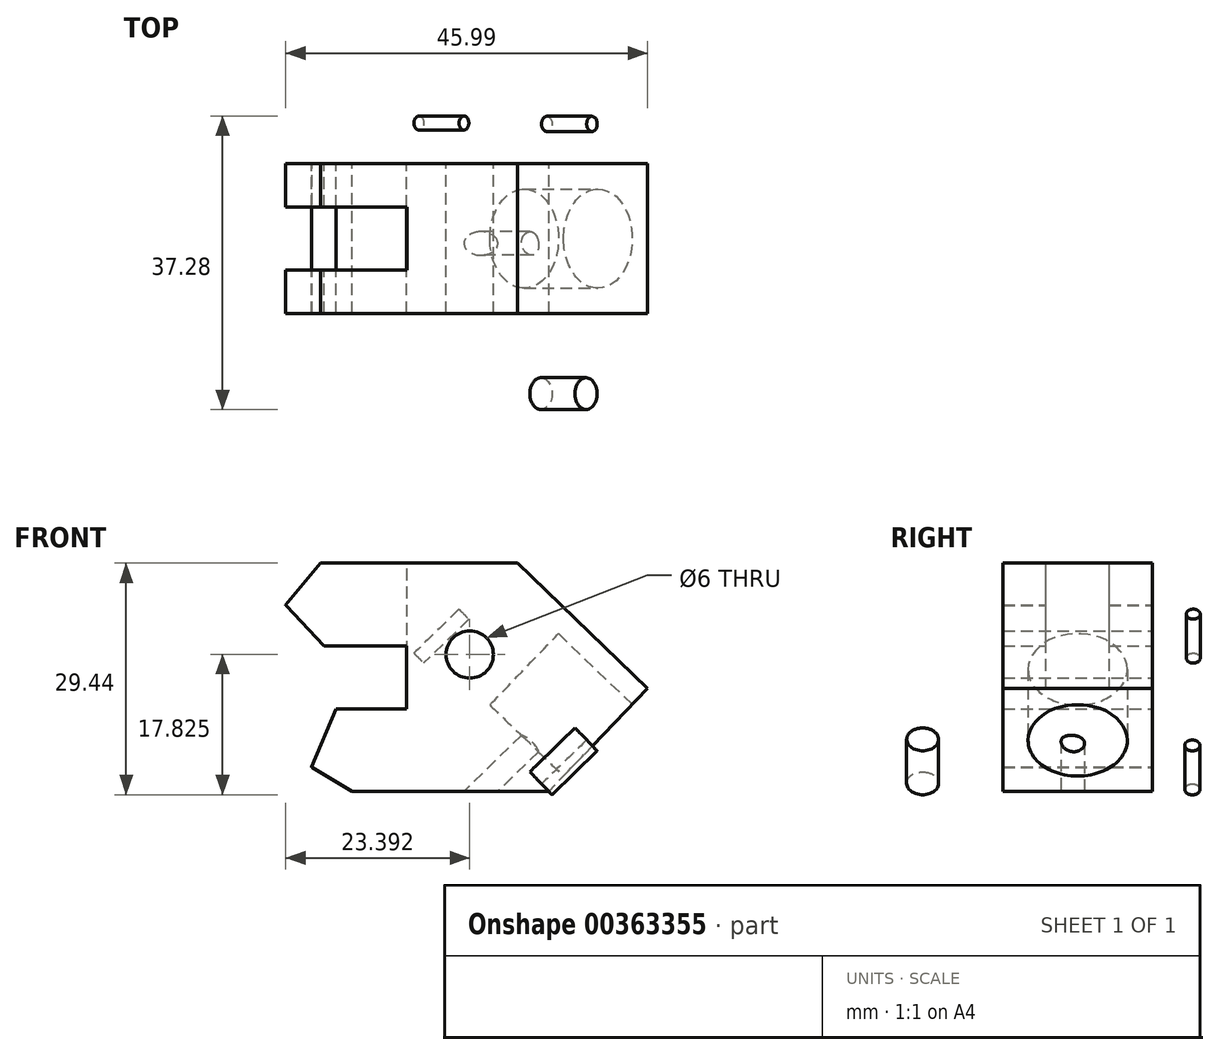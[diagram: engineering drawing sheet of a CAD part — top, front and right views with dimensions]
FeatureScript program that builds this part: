
annotation { "Feature Type Name" : "Feature", "Feature Type Description" : "" }
export const myFeature = defineFeature(function(context is Context, id is Id, definition is map)
    precondition{}
    {
        {
            var Q0;
            Q0=qCreatedBy(makeId("Front.planeOp"),FACE);
            var sketch = newSketch(context, id + "F0", { "sketchPlane" : qUnion([Q0])});
            skLineSegment(sketch, "E0", {"start": v(-71.85, 9.4) * mm, "end": v(-46.85, 9.4) * mm});
            skLineSegment(sketch, "E1", {"start": v(-67.85, -19.6) * mm, "end": v(-42.85, -19.6) * mm});
            skLineSegment(sketch, "E2", {"start": v(-46.85, 9.4) * mm, "end": v(-30.29, -6.55) * mm});
            skLineSegment(sketch, "E3", {"start": v(-30.29, -6.55) * mm, "end": v(-42.85, -19.6) * mm});
            skLineSegment(sketch, "E4", {"start": v(-60.89, -1.1) * mm, "end": v(-60.89, -9.1) * mm});
            skLineSegment(sketch, "E5", {"start": v(-71.39, -1.1) * mm, "end": v(-60.89, -1.1) * mm});
            skLineSegment(sketch, "E6", {"start": v(-69.89, -9.1) * mm, "end": v(-60.89, -9.1) * mm});
            skArc(sketch, "E7", {"start": v(-76.28, 4.05) * mm, "mid": v(-76.27, 4.04) * mm, "end": v(-76.25, 4.02) * mm});
            skArc(sketch, "E8", {"start": v(-76.25, 4.02) * mm, "mid": v(-76.25, 4.02) * mm, "end": v(-76.25, 4.02) * mm});
            skLineSegment(sketch, "E9", {"start": v(-71.85, 9.4) * mm, "end": v(-76.28, 4.05) * mm});
            skLineSegment(sketch, "E10", {"start": v(-76.28, 4.05) * mm, "end": v(-71.39, -1.1) * mm});
            skArc(sketch, "E11", {"start": v(-73, -16.52) * mm, "mid": v(-72.96, -16.53) * mm, "end": v(-72.93, -16.54) * mm});
            skArc(sketch, "E12", {"start": v(-72.93, -16.54) * mm, "mid": v(-72.93, -16.55) * mm, "end": v(-72.94, -16.55) * mm});
            skLineSegment(sketch, "E13", {"start": v(-69.89, -9.1) * mm, "end": v(-73, -16.52) * mm});
            skLineSegment(sketch, "E14", {"start": v(-73, -16.52) * mm, "end": v(-67.85, -19.6) * mm});
            skCircle(sketch, "E15", {"center": v(-52.89, -2.22) * mm, "radius": 3 * mm});
            skSolve(sketch);
        }
        {
            var Q0;
            Q0=makeQuery(id+"F0.imprint","IMPRINT",FACE,{"disambiguationData":[TD([[makeQuery(id+"F0.imprint","IMPRINT",EDGE,{"derivedFrom":sQuery(id+"F0.wireOp",EDGE,"E0")}),-1.0]])]});
            extrude(context, id + "F1", {"entities" : qUnion([Q0]), "depth" : 19 * mm});
        }
        {
            var Q0;
            Q0=makeQuery(id+"F1.opExtrude","SWEPT_FACE",FACE,{"disambiguationData":[OSD([sQuery(id+"F0.wireOp",EDGE,"E0")])]});
            var sketch = newSketch(context, id + "F2", { "sketchPlane" : qUnion([Q0])});
            skLineSegment(sketch, "E16", {"start": v(-29.52, -5.5) * mm, "end": v(-97.4, -5.5) * mm});
            skLineSegment(sketch, "E17", {"start": v(-28.86, -13.5) * mm, "end": v(-100.5, -13.5) * mm});
            skLineSegment(sketch, "E18", {"start": v(-97.4, -5.5) * mm, "end": v(-97.4, -13.5) * mm});
            skLineSegment(sketch, "E19", {"start": v(-60.85, -5.5) * mm, "end": v(-60.85, -13.5) * mm});
            skSolve(sketch);
        }
        {
            var Q0;
            {var subQ0=sQuery(id+"F2.wireOp",EDGE,"E19");Q0=makeQuery(id+"F2.imprint","IMPRINT",FACE,{"disambiguationData":[TD([[makeQuery(id+"F2.imprint","IMPRINT",EDGE,{"derivedFrom":subQ0}),-1.0]])]});}
            var Q1;
            {var subQ0=sQuery(id+"F2.wireOp",EDGE,"E18");Q1=makeQuery(id+"F2.imprint","IMPRINT",FACE,{"disambiguationData":[TD([[makeQuery(id+"F2.imprint","IMPRINT",EDGE,{"derivedFrom":subQ0}),1.0]])]});}
            extrude(context, id + "F3", {"entities" : qUnion([Q0, Q1]), "operationType" : NewBodyOperationType.REMOVE, "oppositeDirection" : true, "depth" : 16 * mm});
        }
        {
            var Q0;
            Q0=makeQuery(id+"F1.opExtrude","SWEPT_FACE",FACE,{"disambiguationData":[OSD([sQuery(id+"F0.wireOp",EDGE,"E3")])]});
            var sketch = newSketch(context, id + "F4", { "sketchPlane" : qUnion([Q0])});
            skCircle(sketch, "E20", {"center": v(-9.5, -34.85) * mm, "radius": 6.3 * mm});
            skSolve(sketch);
        }
        {
            var Q0;
            Q0 = qSketchRegion(id + "F4", true);
            var Q1;
            {var subQ0=sQuery(id+"F0.wireOp",EDGE,"obgSHjAs-CF7U-fFNJ-GP6A-8ZxQo6zeKuEo");Q1=makeQuery(id+"F1.opExtrude","SWEPT_FACE",FACE,{"disambiguationData":[OSD([subQ0]),TDD([makeQuery(id+"F0.imprint","IMPRINT",EDGE,{"disambiguationData":[TD([[makeQuery(id+"F0.imprint","INTERSECT",VERTEX,{"derivedFrom":[sQuery(id+"F0.wireOp",EDGE,"E4"),subQ0]}),1.0]])],"derivedFrom":subQ0})])]});}
            extrude(context, id + "F5", {"entities" : qUnion([Q0, Q1]), "operationType" : NewBodyOperationType.REMOVE, "oppositeDirection" : true, "depth" : 13 * mm});
        }
        {
            var Q0;
            Q0=makeQuery(id+"F1.opExtrude","CAP_VERTEX",VERTEX,{"disambiguationData":[OSD([sQuery(id+"F0.wireOp",EDGE,"E1"),sQuery(id+"F0.wireOp",EDGE,"E3")])],"isStart":false});
            var Q1;
            Q1=makeQuery(id+"F1.opExtrude","CAP_VERTEX",VERTEX,{"disambiguationData":[OSD([sQuery(id+"F0.wireOp",EDGE,"E1"),sQuery(id+"F0.wireOp",EDGE,"E3")])],"isStart":true});
            var Q2;
            Q2=makeQuery(id+"F1.opExtrude","CAP_VERTEX",VERTEX,{"disambiguationData":[OSD([sQuery(id+"F0.wireOp",EDGE,"E4"),sQuery(id+"F0.wireOp",EDGE,"E5")])],"isStart":false});
            cPlane(context, id + "F6", {"entities" : qUnion([Q0, Q1, Q2]), "cplaneType" : CPlaneType.THREE_POINT, "offset" : 25 * mm, "width" : 150 * mm, "height" : 150 * mm});
        }
        {
            var Q0;
            Q0=qCreatedBy(id+"F6.planeOp",FACE);
            var sketch = newSketch(context, id + "F7", { "sketchPlane" : qUnion([Q0])});
            skCircle(sketch, "E21", {"center": v(-5.07, 16.23) * mm, "radius": 0.96 * mm});
            skCircle(sketch, "E22", {"center": v(-5.18, 39.52) * mm, "radius": 0.89 * mm});
            skCircle(sketch, "E23", {"center": v(29.2, 17.3) * mm, "radius": 2.02 * mm});
            skSolve(sketch);
        }
        {
            var Q0;
            Q0=makeQuery(id+"F7.imprint","IMPRINT",FACE,{"disambiguationData":[TD([[makeQuery(id+"F7.imprint","IMPRINT",EDGE,{"derivedFrom":sQuery(id+"F7.wireOp",EDGE,"E23")}),1.0]])]});
            var Q1;
            Q1=makeQuery(id+"F7.imprint","IMPRINT",FACE,{"disambiguationData":[TD([[makeQuery(id+"F7.imprint","IMPRINT",EDGE,{"derivedFrom":sQuery(id+"F7.wireOp",EDGE,"E21")}),1.0]])]});
            var Q2;
            Q2=makeQuery(id+"F7.imprint","IMPRINT",FACE,{"disambiguationData":[TD([[makeQuery(id+"F7.imprint","IMPRINT",EDGE,{"derivedFrom":sQuery(id+"F7.wireOp",EDGE,"E22")}),1.0]])]});
            extrude(context, id + "F8", {"entities" : qUnion([Q0, Q1, Q2]), "oppositeDirection" : true, "depth" : 8 * mm});
        }
        {
            var Q0;
            Q0=makeQuery(id+"F8.opExtrude","CAP_FACE",FACE,{"disambiguationData":[OSD([sQuery(id+"F7.wireOp",EDGE,"E23")])],"isStart":false});
            var sketch = newSketch(context, id + "F9", { "sketchPlane" : qUnion([Q0])});
            skCircle(sketch, "E24", {"center": v(-10.12, 21.9) * mm, "radius": 1.5 * mm});
            skLineSegment(sketch, "E25", {"start": v(-10.12, 15.9) * mm, "end": v(-10.12, 30.7) * mm});
            skCircle(sketch, "E26", {"center": v(-10.12, 21.9) * mm, "radius": 3 * mm});
            skSolve(sketch);
        }
        {
            var Q0;
            {var subQ0=sQuery(id+"F9.wireOp",EDGE,"E25");var subQ1=sQuery(id+"F9.wireOp",EDGE,"E24");var subQ2=makeQuery(id+"F9.imprint","INTERSECT",VERTEX,{"disambiguationData":[OD(0.0)],"derivedFrom":[subQ1,subQ0]});Q0=makeQuery(id+"F9.imprint","IMPRINT",FACE,{"disambiguationData":[TD([[makeQuery(id+"F9.imprint","IMPRINT",EDGE,{"disambiguationData":[TD([[subQ2,-1.0]])],"derivedFrom":subQ1}),1.0]])]});}
            var Q1;
            {var subQ0=sQuery(id+"F9.wireOp",EDGE,"E25");var subQ1=sQuery(id+"F9.wireOp",EDGE,"E24");var subQ2=makeQuery(id+"F9.imprint","INTERSECT",VERTEX,{"disambiguationData":[OD(0.0)],"derivedFrom":[subQ1,subQ0]});Q1=makeQuery(id+"F9.imprint","IMPRINT",FACE,{"disambiguationData":[TD([[makeQuery(id+"F9.imprint","IMPRINT",EDGE,{"disambiguationData":[TD([[subQ2,1.0]])],"derivedFrom":subQ1}),1.0]])]});}
            extrude(context, id + "F10", {"entities" : qUnion([Q0, Q1]), "operationType" : NewBodyOperationType.ADD, "oppositeDirection" : true, "depth" : 25 * mm});
        }
        {
            var Q0;
            Q0=makeQuery(id+"F10.opExtrude","CAP_FACE",FACE,{"disambiguationData":[OSD([sQuery(id+"F9.wireOp",EDGE,"E24")])],"isStart":false});
            var sketch = newSketch(context, id + "F11", { "sketchPlane" : qUnion([Q0])});
            skCircle(sketch, "E27", {"center": v(10.12, 21.9) * mm, "radius": 3 * mm});
            skLineSegment(sketch, "E28", {"start": v(10.12, 21.9) * mm, "end": v(10.12, -18.39) * mm});
            skSolve(sketch);
        }
        {
            var Q0;
            Q0=makeQuery(id+"F11.imprint","IMPRINT",FACE,{"disambiguationData":[TD([[makeQuery(id+"F11.imprint","IMPRINT",EDGE,{"derivedFrom":makeQuery(id+"F10.opExtrude","CAP_EDGE",EDGE,{"disambiguationData":[OSD([sQuery(id+"F9.wireOp",EDGE,"E24")])],"isStart":false})}),-1.0]])]});
            extrude(context, id + "F12", {"entities" : qUnion([Q0]), "operationType" : NewBodyOperationType.REMOVE, "oppositeDirection" : true, "depth" : 25 * mm});
        }
    });
